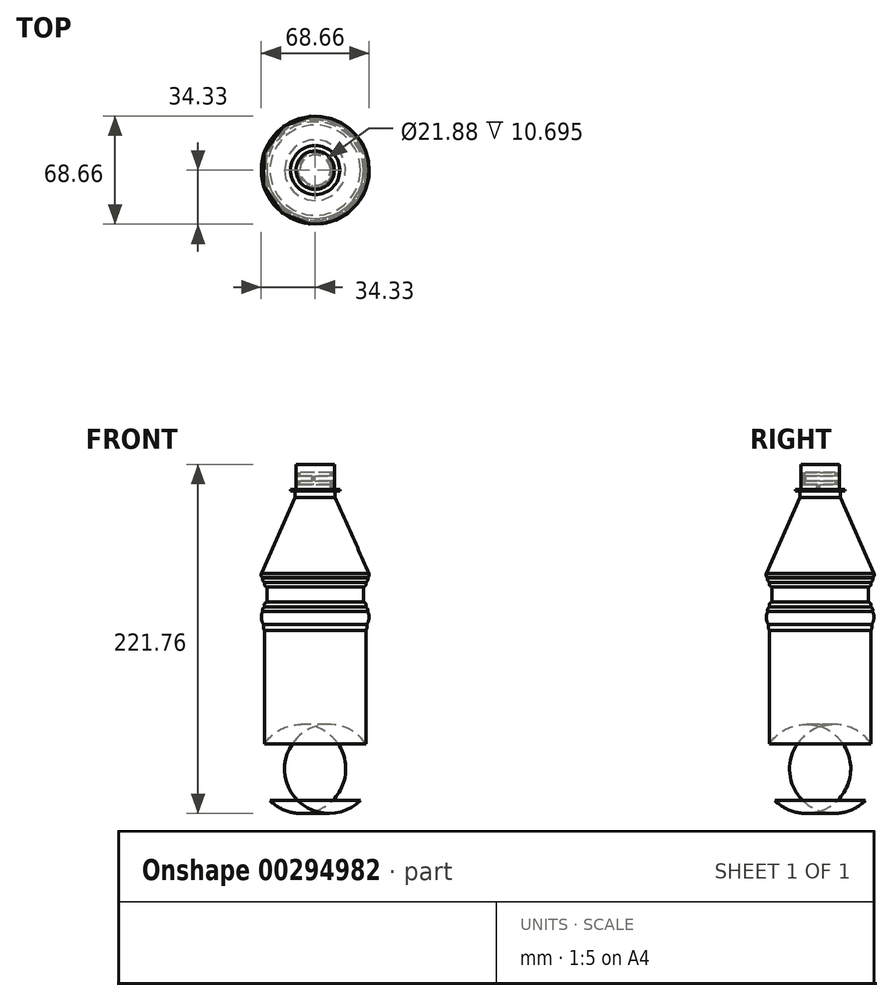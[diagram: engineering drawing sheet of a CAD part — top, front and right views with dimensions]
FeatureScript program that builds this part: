
annotation { "Feature Type Name" : "Feature", "Feature Type Description" : "" }
export const myFeature = defineFeature(function(context is Context, id is Id, definition is map)
    precondition{}
    {
        {
            var Q0;
            Q0=qCreatedBy(makeId("Front.planeOp"),FACE);
            var sketch = newSketch(context, id + "F0", { "sketchPlane" : qUnion([Q0])});
            skPoint(sketch, "E0", {"position": v(0, 76.4) * mm});
            skLineSegment(sketch, "E1", {"start": v(0, 76.4) * mm, "end": v(0, -145.85) * mm});
            skSolve(sketch);
        }
        {
            var Q0;
            Q0=qCreatedBy(makeId("Front.planeOp"),FACE);
            var sketch = newSketch(context, id + "F1", { "sketchPlane" : qUnion([Q0])});
            skLineSegment(sketch, "E2.bottom", {"start": v(0, 76.36) * mm, "end": v(-12.2, 76.36) * mm});
            skLineSegment(sketch, "E2.top", {"start": v(0, 60.35) * mm, "end": v(-12.2, 60.35) * mm});
            skLineSegment(sketch, "E2.left", {"start": v(0, 76.36) * mm, "end": v(0, 60.35) * mm});
            skLineSegment(sketch, "E3", {"start": v(-12.2, 76.36) * mm, "end": v(0, 76.36) * mm});
            skLineSegment(sketch, "E4", {"start": v(-12.2, 76.36) * mm, "end": v(-12.2, 71.05) * mm});
            skLineSegment(sketch, "E5", {"start": v(-12.2, 63.66) * mm, "end": v(-9.65, 63.66) * mm});
            skLineSegment(sketch, "E6", {"start": v(-12.2, 65.74) * mm, "end": v(-9.65, 65.74) * mm});
            skLineSegment(sketch, "E7", {"start": v(-9.65, 65.74) * mm, "end": v(-9.65, 63.66) * mm});
            skLineSegment(sketch, "E8.trimOffspring", {"start": v(-12.2, 63.66) * mm, "end": v(-12.2, 60.35) * mm});
            skLineSegment(sketch, "E9", {"start": v(-9.65, 71.05) * mm, "end": v(-9.65, 68.97) * mm});
            skLineSegment(sketch, "E10.bottom", {"start": v(-12.2, 71.05) * mm, "end": v(-9.65, 71.05) * mm});
            skLineSegment(sketch, "E10.top", {"start": v(-12.2, 68.97) * mm, "end": v(-9.65, 68.97) * mm});
            skLineSegment(sketch, "E11.trimOffspring", {"start": v(-12.2, 68.97) * mm, "end": v(-12.2, 65.74) * mm});
            skPoint(sketch, "E12.orphan", {"position": v(-9.65, 76.36) * mm});
            skLineSegment(sketch, "E13", {"start": v(-9.65, 76.36) * mm, "end": v(-9.65, 60.35) * mm});
            skPoint(sketch, "E13.endSnap0", {"position": v(-9.65, 64.7) * mm});
            skSolve(sketch);
        }
        {
            var Q0;
            Q0=qCreatedBy(makeId("Front.planeOp"),FACE);
            var sketch = newSketch(context, id + "F2", { "sketchPlane" : qUnion([Q0])});
            skLineSegment(sketch, "E14.bottom", {"start": v(0, 60.34) * mm, "end": v(-15.62, 60.34) * mm});
            skLineSegment(sketch, "E14.top", {"start": v(0, 59.32) * mm, "end": v(-15.62, 59.32) * mm});
            skLineSegment(sketch, "E14.left", {"start": v(0, 60.34) * mm, "end": v(0, 59.32) * mm});
            skLineSegment(sketch, "E14.right", {"start": v(-15.62, 60.34) * mm, "end": v(-15.62, 59.32) * mm});
            skSolve(sketch);
        }
        {
            var Q0;
            Q0=qCreatedBy(makeId("Front.planeOp"),FACE);
            var sketch = newSketch(context, id + "F3", { "sketchPlane" : qUnion([Q0])});
            skLineSegment(sketch, "E15.bottom", {"start": v(0, 59.32) * mm, "end": v(-12.74, 59.32) * mm});
            skLineSegment(sketch, "E15.top", {"start": v(0, 55.25) * mm, "end": v(-12.74, 55.25) * mm});
            skLineSegment(sketch, "E15.left", {"start": v(0, 59.32) * mm, "end": v(0, 55.25) * mm});
            skLineSegment(sketch, "E15.right", {"start": v(-12.74, 59.32) * mm, "end": v(-12.74, 55.25) * mm});
            skSolve(sketch);
        }
        {
            var Q0;
            Q0=qCreatedBy(makeId("Front.planeOp"),FACE);
            var sketch = newSketch(context, id + "F4", { "sketchPlane" : qUnion([Q0])});
            skPoint(sketch, "E16", {"position": v(0, 4.4) * mm});
            skLineSegment(sketch, "E17", {"start": v(0, 4.4) * mm, "end": v(-33.5, 4.4) * mm});
            skLineSegment(sketch, "E18", {"start": v(-34.2, 6.89) * mm, "end": v(-12.74, 55.26) * mm});
            skLineSegment(sketch, "E19", {"start": v(-12.74, 55.26) * mm, "end": v(0, 55.26) * mm});
            skLineSegment(sketch, "E20", {"start": v(0, 55.26) * mm, "end": v(0, 4.4) * mm});
            skPoint(sketch, "E21.visualSharp", {"position": v(-35.3, 4.4) * mm});
            skPoint(sketch, "E22", {"position": v(-33.5, 4.4) * mm});
            skPoint(sketch, "E23", {"position": v(-34.04, 7.25) * mm});
            skArc(sketch, "E24", {"start": v(-34.04, 7.25) * mm, "mid": v(-34.29, 5.73) * mm, "end": v(-33.5, 4.4) * mm});
            skSolve(sketch);
        }
        {
            var Q0;
            Q0=qCreatedBy(makeId("Front.planeOp"),FACE);
            var sketch = newSketch(context, id + "F5", { "sketchPlane" : qUnion([Q0])});
            skPoint(sketch, "E25", {"position": v(-156.55, 4.3) * mm});
            skArc(sketch, "E26", {"start": v(-156.55, 4.3) * mm, "mid": v(-157.4, 2.7) * mm, "end": v(-156.55, 1.09) * mm});
            skLineSegment(sketch, "E27", {"start": v(0, 4.3) * mm, "end": v(0, -1.54) * mm});
            skLineSegment(sketch, "E28", {"start": v(0, -1.54) * mm, "end": v(-30.73, -1.54) * mm});
            skLineSegment(sketch, "E29", {"start": v(0, 4.3) * mm, "end": v(-33.27, 4.3) * mm});
            skArc(sketch, "E30", {"start": v(-33.27, 4.3) * mm, "mid": v(-33.25, 2.47) * mm, "end": v(-31.8, 1.35) * mm});
            skArc(sketch, "E31", {"start": v(-31.8, 1.35) * mm, "mid": v(-32.13, -0.42) * mm, "end": v(-30.73, -1.54) * mm});
            skPoint(sketch, "E32.orphan", {"position": v(-33.78, -1.54) * mm});
            skSolve(sketch);
        }
        {
            var Q0;
            Q0=qCreatedBy(makeId("Front.planeOp"),FACE);
            var sketch = newSketch(context, id + "F6", { "sketchPlane" : qUnion([Q0])});
            skLineSegment(sketch, "E33", {"start": v(0, -1.6) * mm, "end": v(0, -11.24) * mm});
            skLineSegment(sketch, "E34", {"start": v(0, -1.6) * mm, "end": v(-30.69, -1.6) * mm});
            skLineSegment(sketch, "E35", {"start": v(0, -11.24) * mm, "end": v(-30.68, -11.24) * mm});
            skLineSegment(sketch, "E36", {"start": v(-30.68, -11.24) * mm, "end": v(-30.69, -1.6) * mm});
            skSolve(sketch);
        }
        {
            var Q0;
            Q0=qCreatedBy(makeId("Front.planeOp"),FACE);
            var sketch = newSketch(context, id + "F7", { "sketchPlane" : qUnion([Q0])});
            skPoint(sketch, "E37", {"position": v(104.6, -17.66) * mm});
            skArc(sketch, "E38", {"start": v(104.6, -17.66) * mm, "mid": v(105.45, -16.05) * mm, "end": v(104.6, -14.45) * mm});
            skPoint(sketch, "E39", {"position": v(-101.02, 2.82) * mm});
            skArc(sketch, "E40", {"start": v(-101.02, 2.82) * mm, "mid": v(-101.86, 1.21) * mm, "end": v(-101.02, -0.4) * mm});
            skLineSegment(sketch, "E41.MirrorCS", {"start": v(0, -17.02) * mm, "end": v(-33.26, -17.02) * mm});
            skPoint(sketch, "E42.MirrorP", {"position": v(-33.8, -11.38) * mm});
            skLineSegment(sketch, "E43.MirrorCS", {"start": v(0, -17.02) * mm, "end": v(0, -11.2) * mm});
            skLineSegment(sketch, "E44.MirrorCS", {"start": v(0, -11.2) * mm, "end": v(-30.68, -11.2) * mm});
            skArc(sketch, "E45.MirrorCS", {"start": v(-31.82, -14.21) * mm, "mid": v(-32.23, -12.34) * mm, "end": v(-30.68, -11.2) * mm});
            skArc(sketch, "E46.MirrorCS", {"start": v(-33.26, -17.02) * mm, "mid": v(-33.18, -15.3) * mm, "end": v(-31.82, -14.21) * mm});
            skSolve(sketch);
        }
        {
            var Q0;
            Q0=qCreatedBy(makeId("Front.planeOp"),FACE);
            var sketch = newSketch(context, id + "F8", { "sketchPlane" : qUnion([Q0])});
            skLineSegment(sketch, "E47", {"start": v(0, -17.06) * mm, "end": v(0, -25.44) * mm});
            skLineSegment(sketch, "E48", {"start": v(0, -17.06) * mm, "end": v(-33.28, -17.06) * mm});
            skLineSegment(sketch, "E49", {"start": v(0, -25.44) * mm, "end": v(-32.77, -25.44) * mm});
            skArc(sketch, "E50", {"start": v(-33.28, -17.06) * mm, "mid": v(-34.18, -21.32) * mm, "end": v(-32.77, -25.44) * mm});
            skSolve(sketch);
        }
        {
            var Q0;
            Q0=qCreatedBy(makeId("Front.planeOp"),FACE);
            var sketch = newSketch(context, id + "F9", { "sketchPlane" : qUnion([Q0])});
            skLineSegment(sketch, "E51", {"start": v(0, -25.47) * mm, "end": v(0, -29.03) * mm});
            skLineSegment(sketch, "E52", {"start": v(0, -25.47) * mm, "end": v(-32.72, -25.47) * mm});
            skLineSegment(sketch, "E53", {"start": v(0, -29.03) * mm, "end": v(-32.26, -29.03) * mm});
            skArc(sketch, "E54", {"start": v(-32.72, -25.47) * mm, "mid": v(-32.9, -27.3) * mm, "end": v(-32.26, -29.03) * mm});
            skSolve(sketch);
        }
        {
            var Q0;
            Q0=qCreatedBy(makeId("Front.planeOp"),FACE);
            var sketch = newSketch(context, id + "F10", { "sketchPlane" : qUnion([Q0])});
            skLineSegment(sketch, "E55", {"start": v(0, -29.07) * mm, "end": v(0, -101.2) * mm});
            skLineSegment(sketch, "E56", {"start": v(0, -29.07) * mm, "end": v(-32.25, -29.07) * mm});
            skLineSegment(sketch, "E57", {"start": v(-32.25, -29.07) * mm, "end": v(-32.25, -101.2) * mm});
            skLineSegment(sketch, "E58", {"start": v(0, -101.2) * mm, "end": v(-32.25, -101.2) * mm});
            skSolve(sketch);
        }
        {
            var Q0;
            Q0=qCreatedBy(makeId("Front.planeOp"),FACE);
            var sketch = newSketch(context, id + "F11", { "sketchPlane" : qUnion([Q0])});
            skLineSegment(sketch, "E59", {"start": v(0, -101.2) * mm, "end": v(0, -137.28) * mm});
            skLineSegment(sketch, "E60", {"start": v(0, -101.2) * mm, "end": v(-32.26, -101.2) * mm});
            skLineSegment(sketch, "E61", {"start": v(0, -137.28) * mm, "end": v(-28.7, -137.28) * mm});
            skArc(sketch, "E62", {"start": v(-32.26, -101.2) * mm, "mid": v(-37.02, -119.89) * mm, "end": v(-28.7, -137.28) * mm});
            skSolve(sketch);
        }
        {
            var Q0;
            Q0=makeQuery(id+"F1.imprint","IMPRINT",FACE,{"disambiguationData":[TD([[makeQuery(id+"F1.imprint","IMPRINT",EDGE,{"derivedFrom":sQuery(id+"F1.wireOp",EDGE,"E2.bottom")}),1.0]])]});
            var Q1;
            Q1=makeQuery(id+"F2.imprint","IMPRINT",FACE,{"disambiguationData":[TD([[makeQuery(id+"F2.imprint","IMPRINT",EDGE,{"derivedFrom":sQuery(id+"F2.wireOp",EDGE,"E14.bottom")}),1.0]])]});
            var Q2;
            Q2=makeQuery(id+"F3.imprint","IMPRINT",FACE,{"disambiguationData":[TD([[makeQuery(id+"F3.imprint","IMPRINT",EDGE,{"derivedFrom":sQuery(id+"F3.wireOp",EDGE,"E15.bottom")}),1.0]])]});
            var Q3;
            {var subQ5=sQuery(id+"F4.wireOp",EDGE,"E17");Q3=makeQuery(id+"F4.imprint","IMPRINT",FACE,{"disambiguationData":[TD([[makeQuery(id+"F4.imprint","IMPRINT",EDGE,{"derivedFrom":subQ5}),-1.0]])]});}
            var Q4;
            Q4=makeQuery(id+"F5.imprint","IMPRINT",FACE,{"disambiguationData":[TD([[makeQuery(id+"F5.imprint","IMPRINT",EDGE,{"derivedFrom":sQuery(id+"F5.wireOp",EDGE,"E27")}),-1.0]])]});
            var Q5;
            Q5=makeQuery(id+"F6.imprint","IMPRINT",FACE,{"disambiguationData":[TD([[makeQuery(id+"F6.imprint","IMPRINT",EDGE,{"derivedFrom":sQuery(id+"F6.wireOp",EDGE,"E33")}),-1.0]])]});
            var Q6;
            Q6=sQuery(id+"F0.wireOp",EDGE,"E1");
            revolve(context, id + "F12", {"entities" : qUnion([Q0, Q1, Q2, Q3, Q4, Q5]), "axis" : qUnion([Q6]), "revolveType" : RevolveType.FULL});
        }
        {
            var Q0;
            Q0=makeQuery(id+"F8.imprint","IMPRINT",FACE,{"disambiguationData":[TD([[makeQuery(id+"F8.imprint","IMPRINT",EDGE,{"derivedFrom":sQuery(id+"F8.wireOp",EDGE,"E47")}),-1.0]])]});
            var Q1;
            Q1=makeQuery(id+"F9.imprint","IMPRINT",FACE,{"disambiguationData":[TD([[makeQuery(id+"F9.imprint","IMPRINT",EDGE,{"derivedFrom":sQuery(id+"F9.wireOp",EDGE,"E51")}),-1.0]])]});
            var Q2;
            Q2=makeQuery(id+"F10.imprint","IMPRINT",FACE,{"disambiguationData":[TD([[makeQuery(id+"F10.imprint","IMPRINT",EDGE,{"derivedFrom":sQuery(id+"F10.wireOp",EDGE,"E55")}),-1.0]])]});
            var Q3;
            Q3=makeQuery(id+"F11.imprint","IMPRINT",FACE,{"disambiguationData":[TD([[makeQuery(id+"F11.imprint","IMPRINT",EDGE,{"derivedFrom":sQuery(id+"F11.wireOp",EDGE,"E59")}),-1.0]])]});
            var Q4;
            Q4=sQuery(id+"F0.wireOp",EDGE,"E1");
            revolve(context, id + "F13", {"entities" : qUnion([Q0, Q1, Q2, Q3]), "axis" : qUnion([Q4]), "revolveType" : RevolveType.FULL});
        }
        {
            var Q0;
            Q0=makeQuery(id+"F7.imprint","IMPRINT",FACE,{"disambiguationData":[TD([[makeQuery(id+"F7.imprint","IMPRINT",EDGE,{"derivedFrom":sQuery(id+"F7.wireOp",EDGE,"E41.MirrorCS")}),-1.0]])]});
            var Q1;
            Q1=sQuery(id+"F0.wireOp",EDGE,"E1");
            revolve(context, id + "F14", {"operationType" : NewBodyOperationType.ADD, "entities" : qUnion([Q0]), "axis" : qUnion([Q1]), "revolveType" : RevolveType.FULL});
        }
        {
            var Q0;
            Q0=makeQuery(id+"F12.opRevolve","SWEPT_FACE",FACE,{"disambiguationData":[OSD([sQuery(id+"F1.wireOp",EDGE,"E2.bottom")])]});
            var sketch = newSketch(context, id + "F15", { "sketchPlane" : qUnion([Q0])});
            skCircle(sketch, "E63", {"center": v(0, 0) * mm, "radius": 10.94 * mm});
            skCircle(sketch, "E64", {"center": v(0, 0) * mm, "radius": 13.19 * mm});
            skSolve(sketch);
        }
        {
            var Q0;
            Q0=makeQuery(id+"F15.imprint","IMPRINT",FACE,{"disambiguationData":[TD([[makeQuery(id+"F15.imprint","IMPRINT",EDGE,{"derivedFrom":sQuery(id+"F15.wireOp",EDGE,"E63")}),-1.0]])]});
            extrude(context, id + "F16", {"entities" : qUnion([Q0]), "operationType" : NewBodyOperationType.ADD, "oppositeDirection" : true, "depth" : 16 * mm});
        }
        {
            var Q0;
            Q0=makeQuery(id+"F1.imprint","IMPRINT",FACE,{"disambiguationData":[TD([[makeQuery(id+"F1.imprint","IMPRINT",EDGE,{"derivedFrom":sQuery(id+"F1.wireOp",EDGE,"E2.left")}),-1.0]])]});
            var Q1;
            Q1=sQuery(id+"F1.wireOp",EDGE,"E2.left");
            revolve(context, id + "F17", {"entities" : qUnion([Q0]), "axis" : qUnion([Q1]), "revolveType" : RevolveType.FULL});
        }
        {
            var Q0;
            {var subQ0=sQuery(id+"F1.wireOp",EDGE,"E4");Q0=makeQuery(id+"F1.imprint","IMPRINT",FACE,{"disambiguationData":[TD([[makeQuery(id+"F1.imprint","IMPRINT",EDGE,{"derivedFrom":subQ0}),1.0]])]});}
            var Q1;
            Q1=sQuery(id+"F1.wireOp",EDGE,"E2.left");
            revolve(context, id + "F18", {"operationType" : NewBodyOperationType.ADD, "entities" : qUnion([Q0]), "axis" : qUnion([Q1]), "revolveType" : RevolveType.ONE_DIRECTION, "angle" : 350 * degree});
        }
        {
            var Q0;
            {var subQ4=sQuery(id+"F1.wireOp",EDGE,"E5");Q0=makeQuery(id+"F1.imprint","IMPRINT",FACE,{"disambiguationData":[TD([[makeQuery(id+"F1.imprint","IMPRINT",EDGE,{"derivedFrom":subQ4}),-1.0]])]});}
            var Q1;
            Q1=sQuery(id+"F1.wireOp",EDGE,"E2.left");
            revolve(context, id + "F19", {"operationType" : NewBodyOperationType.ADD, "entities" : qUnion([Q0]), "axis" : qUnion([Q1]), "revolveType" : RevolveType.TWO_DIRECTIONS, "angle" : 180 * degree, "angleBack" : 190 * degree});
        }
        {
            var Q0;
            {var subQ0=sQuery(id+"F1.wireOp",EDGE,"E6");Q0=makeQuery(id+"F1.imprint","IMPRINT",FACE,{"disambiguationData":[TD([[makeQuery(id+"F1.imprint","IMPRINT",EDGE,{"derivedFrom":subQ0}),1.0]])]});}
            var Q1;
            Q1=sQuery(id+"F1.wireOp",EDGE,"E2.left");
            revolve(context, id + "F20", {"operationType" : NewBodyOperationType.ADD, "entities" : qUnion([Q0]), "axis" : qUnion([Q1]), "revolveType" : RevolveType.TWO_DIRECTIONS, "angle" : 270 * degree, "angleBack" : 280 * degree});
        }
    });
